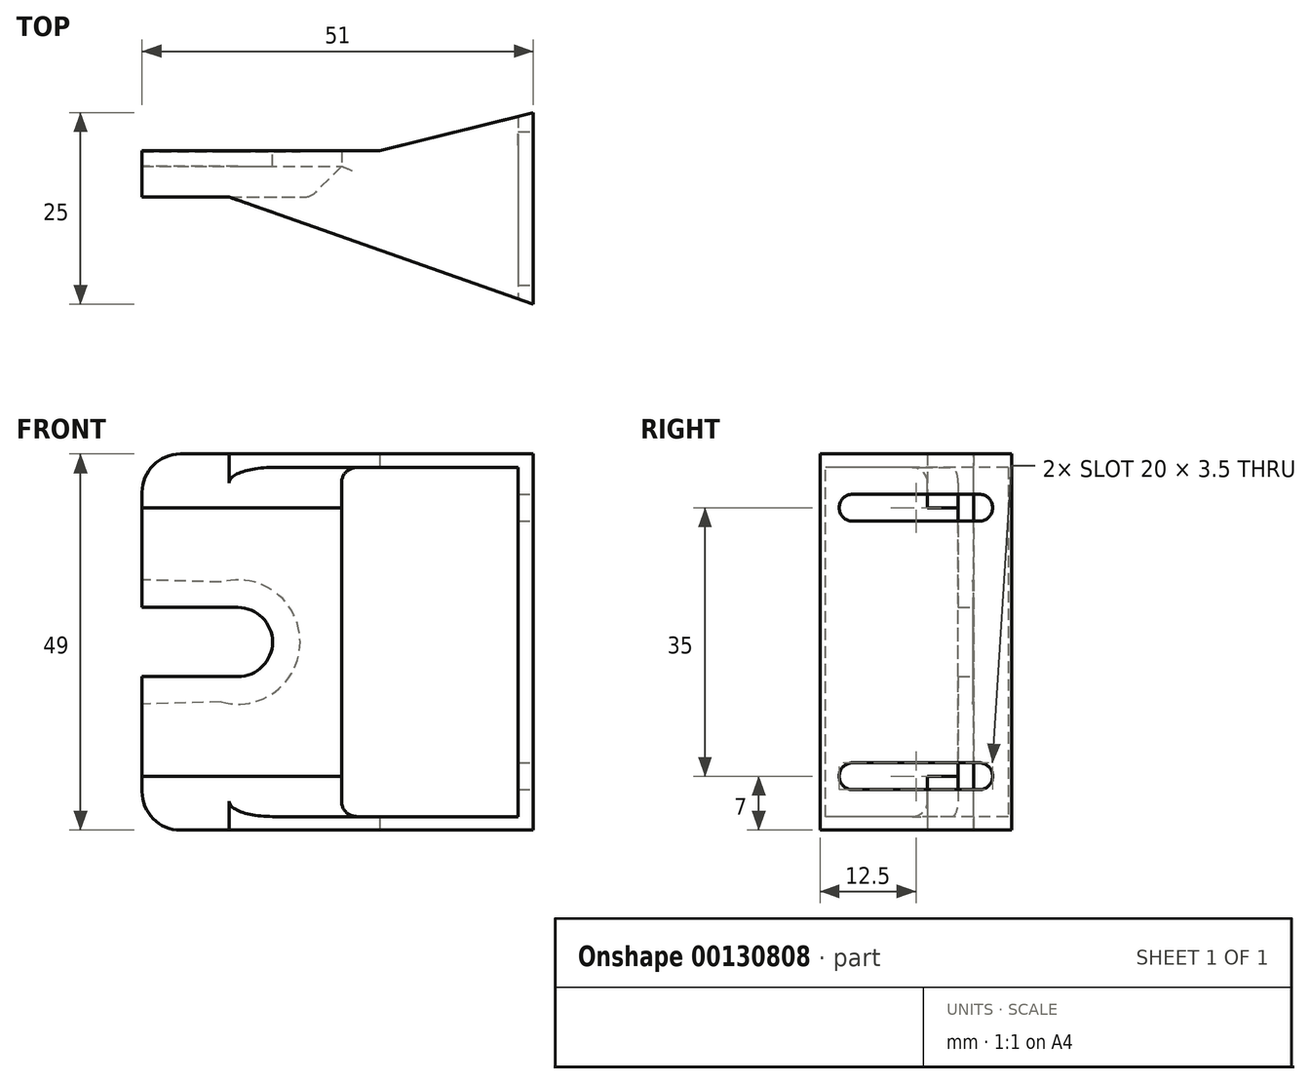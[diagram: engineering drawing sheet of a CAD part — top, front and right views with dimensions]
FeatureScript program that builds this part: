
annotation { "Feature Type Name" : "Feature", "Feature Type Description" : "" }
export const myFeature = defineFeature(function(context is Context, id is Id, definition is map)
    precondition{}
    {
        {
            var Q0;
            Q0=qCreatedBy(makeId("Top.planeOp"),FACE);
            var sketch = newSketch(context, id + "F0", { "sketchPlane" : qUnion([Q0])});
            skLineSegment(sketch, "E0.bottom", {"start": v(0, 2) * mm, "end": v(51, 2) * mm});
            skLineSegment(sketch, "E0.top", {"start": v(0, 0) * mm, "end": v(0, 0) * mm});
            skLineSegment(sketch, "E0.left", {"start": v(0, 2) * mm, "end": v(0, 0) * mm});
            skLineSegment(sketch, "E1", {"start": v(51, 2) * mm, "end": v(51, -18) * mm});
            skLineSegment(sketch, "E2", {"start": v(0, 0) * mm, "end": v(51, -18) * mm});
            skLineSegment(sketch, "E3", {"start": v(51, 2) * mm, "end": v(51, 7) * mm});
            skLineSegment(sketch, "E4", {"start": v(51, 7) * mm, "end": v(31, 2) * mm});
            skSolve(sketch);
        }
        {
            var Q0;
            Q0=makeQuery(id+"F0.imprint","IMPRINT",FACE,{"disambiguationData":[TD([[makeQuery(id+"F0.imprint","IMPRINT",EDGE,{"derivedFrom":sQuery(id+"F0.wireOp",EDGE,"E0.bottom")}),-1.0]])]});
            var Q1;
            {var subQ0=sQuery(id+"F0.wireOp",EDGE,"SCWSvQnW-zgxt-xv1m-XBCz-Pb8vfzgxZMeU");Q1=makeQuery(id+"F0.imprint","IMPRINT",FACE,{"disambiguationData":[TD([[makeQuery(id+"F0.imprint","IMPRINT",EDGE,{"derivedFrom":subQ0}),-1.0]])]});}
            var Q2;
            {var subQ0=sQuery(id+"F0.wireOp",EDGE,"E3");Q2=makeQuery(id+"F0.imprint","IMPRINT",FACE,{"disambiguationData":[TD([[makeQuery(id+"F0.imprint","IMPRINT",EDGE,{"derivedFrom":subQ0}),1.0]])]});}
            extrude(context, id + "F1", {"entities" : qUnion([Q0, Q1, Q2]), "depth" : 49 * mm});
        }
        {
            var Q0;
            Q0=makeQuery(id+"F1.opExtrude","SWEPT_FACE",FACE,{"disambiguationData":[OSD([sQuery(id+"F0.wireOp",EDGE,"E0.bottom")])]});
            var sketch = newSketch(context, id + "F2", { "sketchPlane" : qUnion([Q0])});
            skArc(sketch, "E5", {"start": v(-12.5, 29) * mm, "mid": v(-17, 24.5) * mm, "end": v(-12.5, 20) * mm});
            skPoint(sketch, "E5.centerSnap0", {"position": v(0, 24.5) * mm});
            skLineSegment(sketch, "E6.bottom", {"start": v(-12.5, 20) * mm, "end": v(0.01, 20) * mm});
            skLineSegment(sketch, "E6.top", {"start": v(-12.5, 29) * mm, "end": v(0, 29) * mm});
            skLineSegment(sketch, "E6.right", {"start": v(0.01, 20) * mm, "end": v(0, 29) * mm});
            skSolve(sketch);
        }
        {
            var Q0;
            Q0=makeQuery(id+"F2.imprint","IMPRINT",FACE,{"disambiguationData":[TD([[makeQuery(id+"F2.imprint","IMPRINT",EDGE,{"derivedFrom":sQuery(id+"F2.wireOp",EDGE,"E5")}),1.0]])]});
            extrude(context, id + "F3", {"entities" : qUnion([Q0]), "operationType" : NewBodyOperationType.REMOVE, "endBound" : BoundingType.UP_TO_NEXT, "oppositeDirection" : true, "depth" : 25 * mm});
        }
        {
            var Q0;
            Q0=makeQuery(id+"F1.opExtrude","SWEPT_FACE",FACE,{"disambiguationData":[OSD([sQuery(id+"F0.wireOp",EDGE,"E0.bottom")])]});
            var sketch = newSketch(context, id + "F4", { "sketchPlane" : qUnion([Q0])});
            skLineSegment(sketch, "E7.bottom", {"start": v(-49, 47.25) * mm, "end": v(-26, 47.25) * mm});
            skLineSegment(sketch, "E7.top", {"start": v(-49, 1.75) * mm, "end": v(-26, 1.75) * mm});
            skLineSegment(sketch, "E7.left", {"start": v(-49, 47.25) * mm, "end": v(-49, 1.75) * mm});
            skLineSegment(sketch, "E7.right", {"start": v(-26, 47.25) * mm, "end": v(-26, 1.75) * mm});
            skSolve(sketch);
        }
        {
            var Q0;
            Q0=makeQuery(id+"F4.imprint","IMPRINT",FACE,{"disambiguationData":[TD([[makeQuery(id+"F4.imprint","IMPRINT",EDGE,{"derivedFrom":sQuery(id+"F4.wireOp",EDGE,"E7.bottom")}),-1.0]])]});
            extrude(context, id + "F5", {"entities" : qUnion([Q0]), "operationType" : NewBodyOperationType.REMOVE, "endBound" : BoundingType.SYMMETRIC, "depth" : 50 * mm});
        }
        {
            var Q0;
            Q0=makeQuery(id+"F1.opExtrude","SWEPT_FACE",FACE,{"disambiguationData":[OSD([sQuery(id+"F0.wireOp",EDGE,"E1")])]});
            var sketch = newSketch(context, id + "F6", { "sketchPlane" : qUnion([Q0])});
            skCircle(sketch, "E8", {"center": v(2.75, 42) * mm, "radius": 1.75 * mm});
            skCircle(sketch, "E9", {"center": v(-13.75, 42) * mm, "radius": 1.75 * mm});
            skCircle(sketch, "E10", {"center": v(2.75, 7) * mm, "radius": 1.75 * mm});
            skCircle(sketch, "E11", {"center": v(-13.75, 7) * mm, "radius": 1.75 * mm});
            skLineSegment(sketch, "E12", {"start": v(2.75, 7) * mm, "end": v(2.75, 42) * mm});
            skLineSegment(sketch, "E13", {"start": v(7, 24.5) * mm, "end": v(2.75, 24.5) * mm});
            skPoint(sketch, "E13.endSnap0", {"position": v(7, 24.5) * mm});
            skLineSegment(sketch, "E14", {"start": v(-13.75, 5.25) * mm, "end": v(2.75, 5.25) * mm});
            skLineSegment(sketch, "E15", {"start": v(-13.75, 8.75) * mm, "end": v(2.75, 8.75) * mm});
            skLineSegment(sketch, "E16", {"start": v(2.75, 40.25) * mm, "end": v(-13.75, 40.25) * mm});
            skLineSegment(sketch, "E17", {"start": v(2.75, 43.75) * mm, "end": v(-13.75, 43.75) * mm});
            skSolve(sketch);
        }
        {
            var Q0;
            {var subQ0=sQuery(id+"F6.wireOp",EDGE,"E16");Q0=makeQuery(id+"F6.imprint","IMPRINT",FACE,{"disambiguationData":[TD([[makeQuery(id+"F6.imprint","IMPRINT",EDGE,{"derivedFrom":subQ0}),-1.0]])]});}
            var Q1;
            {var subQ0=sQuery(id+"F6.wireOp",EDGE,"E9");var subQ1=makeQuery(id+"F6.imprint","INTERSECT",VERTEX,{"derivedFrom":[subQ0,sQuery(id+"F6.wireOp",EDGE,"E16")]});Q1=makeQuery(id+"F6.imprint","IMPRINT",FACE,{"disambiguationData":[TD([[makeQuery(id+"F6.imprint","IMPRINT",EDGE,{"disambiguationData":[TD([[subQ1,1.0]])],"derivedFrom":subQ0}),1.0]])]});}
            var Q2;
            {var subQ0=sQuery(id+"F6.wireOp",EDGE,"E8");var subQ1=makeQuery(id+"F6.imprint","INTERSECT",VERTEX,{"derivedFrom":[subQ0,sQuery(id+"F6.wireOp",EDGE,"E16")]});Q2=makeQuery(id+"F6.imprint","IMPRINT",FACE,{"disambiguationData":[TD([[makeQuery(id+"F6.imprint","IMPRINT",EDGE,{"disambiguationData":[TD([[subQ1,1.0]])],"derivedFrom":subQ0}),1.0]])]});}
            var Q3;
            {var subQ0=sQuery(id+"F6.wireOp",EDGE,"E14");Q3=makeQuery(id+"F6.imprint","IMPRINT",FACE,{"disambiguationData":[TD([[makeQuery(id+"F6.imprint","IMPRINT",EDGE,{"derivedFrom":subQ0}),1.0]])]});}
            var Q4;
            {var subQ0=sQuery(id+"F6.wireOp",EDGE,"E11");var subQ1=makeQuery(id+"F6.imprint","INTERSECT",VERTEX,{"derivedFrom":[subQ0,sQuery(id+"F6.wireOp",EDGE,"E14")]});Q4=makeQuery(id+"F6.imprint","IMPRINT",FACE,{"disambiguationData":[TD([[makeQuery(id+"F6.imprint","IMPRINT",EDGE,{"disambiguationData":[TD([[subQ1,1.0]])],"derivedFrom":subQ0}),1.0]])]});}
            var Q5;
            {var subQ0=sQuery(id+"F6.wireOp",EDGE,"E10");var subQ1=makeQuery(id+"F6.imprint","INTERSECT",VERTEX,{"derivedFrom":[subQ0,sQuery(id+"F6.wireOp",EDGE,"E14")]});Q5=makeQuery(id+"F6.imprint","IMPRINT",FACE,{"disambiguationData":[TD([[makeQuery(id+"F6.imprint","IMPRINT",EDGE,{"disambiguationData":[TD([[subQ1,1.0]])],"derivedFrom":subQ0}),1.0]])]});}
            extrude(context, id + "F7", {"entities" : qUnion([Q0, Q1, Q2, Q3, Q4, Q5]), "operationType" : NewBodyOperationType.REMOVE, "endBound" : BoundingType.UP_TO_NEXT, "oppositeDirection" : true, "depth" : 25 * mm});
        }
        {
            var Q0;
            Q0=qCreatedBy(makeId("Front.planeOp"),FACE);
            var sketch = newSketch(context, id + "F8", { "sketchPlane" : qUnion([Q0])});
            skLineSegment(sketch, "E18.bottom", {"start": v(31.05, 47.25) * mm, "end": v(-2.7, 47.25) * mm});
            skLineSegment(sketch, "E18.top", {"start": v(31.05, 1.75) * mm, "end": v(-2.7, 1.75) * mm});
            skLineSegment(sketch, "E18.left", {"start": v(31.05, 47.25) * mm, "end": v(31.05, 1.75) * mm});
            skLineSegment(sketch, "E18.right", {"start": v(-2.7, 47.25) * mm, "end": v(-2.7, 1.75) * mm});
            skSolve(sketch);
        }
        {
            var Q0;
            Q0=qSketchRegion(id+"F8",true);
            extrude(context, id + "F9", {"entities" : qUnion([Q0]), "operationType" : NewBodyOperationType.REMOVE, "endBound" : BoundingType.THROUGH_ALL, "depth" : 25 * mm});
        }
        {
            var Q0;
            {var subQ3=sQuery(id+"F2.wireOp",EDGE,"E5");Q0=makeQuery(id+"F2.imprint","IMPRINT",FACE,{"disambiguationData":[TD([[makeQuery(id+"F2.imprint","IMPRINT",EDGE,{"derivedFrom":subQ3}),-1.0]])]});}
            var sketch = newSketch(context, id + "F10", { "sketchPlane" : qUnion([Q0])});
            skCircle(sketch, "E19", {"center": v(-12.5, 24.5) * mm, "radius": 8.1 * mm});
            skLineSegment(sketch, "E20", {"start": v(-10.32, 32.3) * mm, "end": v(0, 32.6) * mm});
            skLineSegment(sketch, "E21", {"start": v(-10.32, 16.7) * mm, "end": v(0, 16.4) * mm});
            skLineSegment(sketch, "E22", {"start": v(0, 16.4) * mm, "end": v(0, 32.6) * mm});
            skSolve(sketch);
        }
        {
            var Q0;
            Q0=qSketchRegion(id+"F10",true);
            extrude(context, id + "F11", {"entities" : qUnion([Q0]), "operationType" : NewBodyOperationType.REMOVE, "oppositeDirection" : true, "depth" : 0.1 * mm});
        }
        {
            var Q0;
            Q0=makeQuery(id+"F9.boolean.opBoolean","COPY",FACE,{"derivedFrom":makeQuery(id+"F9.opExtrude","CAP_FACE",FACE,{"disambiguationData":[OSD([sQuery(id+"F8.wireOp",EDGE,"E18.bottom"),sQuery(id+"F8.wireOp",EDGE,"E18.top"),sQuery(id+"F8.wireOp",EDGE,"E18.left"),sQuery(id+"F8.wireOp",EDGE,"E18.right")])],"isStart":true})});
            var sketch = newSketch(context, id + "F12", { "sketchPlane" : qUnion([Q0])});
            skLineSegment(sketch, "E23.bottom", {"start": v(0, 49) * mm, "end": v(26, 49) * mm});
            skLineSegment(sketch, "E23.top", {"start": v(0, 42) * mm, "end": v(26, 42) * mm});
            skLineSegment(sketch, "E23.left", {"start": v(0, 49) * mm, "end": v(0, 42) * mm});
            skLineSegment(sketch, "E23.right", {"start": v(26, 49) * mm, "end": v(26, 42) * mm});
            skLineSegment(sketch, "E24.bottom", {"start": v(0, 7) * mm, "end": v(26, 7) * mm});
            skLineSegment(sketch, "E24.top", {"start": v(0, 0) * mm, "end": v(26, 0) * mm});
            skLineSegment(sketch, "E24.left", {"start": v(0, 7) * mm, "end": v(0, 0) * mm});
            skLineSegment(sketch, "E24.right", {"start": v(26, 7) * mm, "end": v(26, 0) * mm});
            skLineSegment(sketch, "E25", {"start": v(0, 42) * mm, "end": v(0, 7) * mm});
            skLineSegment(sketch, "E26", {"start": v(17, 24.5) * mm, "end": v(0, 24.5) * mm});
            skSolve(sketch);
        }
        {
            var Q0;
            {var subQ0=sQuery(id+"F12.wireOp",EDGE,"E23.bottom");Q0=makeQuery(id+"F12.imprint","IMPRINT",FACE,{"disambiguationData":[TD([[makeQuery(id+"F12.imprint","IMPRINT",EDGE,{"derivedFrom":subQ0}),-1.0]])]});}
            var Q1;
            {var subQ0=sQuery(id+"F12.wireOp",EDGE,"E24.top");Q1=makeQuery(id+"F12.imprint","IMPRINT",FACE,{"disambiguationData":[TD([[makeQuery(id+"F12.imprint","IMPRINT",EDGE,{"derivedFrom":subQ0}),1.0]])]});}
            var Q2;
            {var subQ0=sQuery(id+"F12.wireOp",EDGE,"E23.top");Q2=makeQuery(id+"F12.imprint","IMPRINT",FACE,{"disambiguationData":[TD([[makeQuery(id+"F12.imprint","IMPRINT",EDGE,{"derivedFrom":subQ0}),1.0]])]});}
            var Q3;
            {var subQ0=sQuery(id+"F12.wireOp",EDGE,"E24.bottom");Q3=makeQuery(id+"F12.imprint","IMPRINT",FACE,{"disambiguationData":[TD([[makeQuery(id+"F12.imprint","IMPRINT",EDGE,{"derivedFrom":subQ0}),-1.0]])]});}
            extrude(context, id + "F13", {"entities" : qUnion([Q0, Q1, Q2, Q3]), "operationType" : NewBodyOperationType.ADD, "depth" : 4 * mm});
        }
        {
            var Q0;
            Q0=makeQuery(id+"F13.opExtrude","CAP_EDGE",EDGE,{"disambiguationData":[OSD([sQuery(id+"F12.wireOp",EDGE,"E24.right")])],"isStart":false});
            var Q1;
            Q1=makeQuery(id+"F13.opExtrude","CAP_EDGE",EDGE,{"disambiguationData":[OSD([sQuery(id+"F12.wireOp",EDGE,"E23.right")])],"isStart":false});
            chamfer(context, id + "F14", {"entities" : qUnion([Q0, Q1]), "width" : 4 * mm, "tangentPropagation" : true});
        }
        {
            var Q0;
            Q0=makeQuery(id+"F13.boolean.opBoolean","INTERSECT",EDGE,{"derivedFrom":[makeQuery(id+"F9.boolean.opBoolean","MERGE",FACE,{"derivedFrom":[makeQuery(id+"F5.boolean.opBoolean","COPY",FACE,{"derivedFrom":makeQuery(id+"F5.opExtrude","SWEPT_FACE",FACE,{"disambiguationData":[OSD([sQuery(id+"F4.wireOp",EDGE,"E7.top")])]})}),makeQuery(id+"F9.opExtrude","SWEPT_FACE",FACE,{"disambiguationData":[OSD([sQuery(id+"F8.wireOp",EDGE,"E18.top")])]})]}),makeQuery(id+"F13.opExtrude","CAP_FACE",FACE,{"disambiguationData":[OSD([sQuery(id+"F12.wireOp",EDGE,"E24.bottom"),sQuery(id+"F12.wireOp",EDGE,"E24.top"),sQuery(id+"F12.wireOp",EDGE,"E24.left"),sQuery(id+"F12.wireOp",EDGE,"E24.right")])],"isStart":false})]});
            var Q1;
            Q1=makeQuery(id+"F13.boolean.opBoolean","INTERSECT",EDGE,{"derivedFrom":[makeQuery(id+"F9.boolean.opBoolean","MERGE",FACE,{"derivedFrom":[makeQuery(id+"F5.boolean.opBoolean","COPY",FACE,{"derivedFrom":makeQuery(id+"F5.opExtrude","SWEPT_FACE",FACE,{"disambiguationData":[OSD([sQuery(id+"F4.wireOp",EDGE,"E7.bottom")])]})}),makeQuery(id+"F9.opExtrude","SWEPT_FACE",FACE,{"disambiguationData":[OSD([sQuery(id+"F8.wireOp",EDGE,"E18.bottom")])]})]}),makeQuery(id+"F13.opExtrude","CAP_FACE",FACE,{"disambiguationData":[OSD([sQuery(id+"F12.wireOp",EDGE,"E23.bottom"),sQuery(id+"F12.wireOp",EDGE,"E23.top"),sQuery(id+"F12.wireOp",EDGE,"E23.left"),sQuery(id+"F12.wireOp",EDGE,"E23.right")])],"isStart":false})]});
            var Q2;
            Q2=makeQuery(id+"F14.opChamfer","BLEND_EDGE",EDGE,{"blendedFrom":[makeQuery(id+"F13.opExtrude","CAP_EDGE",EDGE,{"disambiguationData":[OSD([sQuery(id+"F12.wireOp",EDGE,"E23.right")])],"isStart":false}),makeQuery(id+"F9.boolean.opBoolean","MERGE",FACE,{"derivedFrom":[makeQuery(id+"F5.boolean.opBoolean","COPY",FACE,{"derivedFrom":makeQuery(id+"F5.opExtrude","SWEPT_FACE",FACE,{"disambiguationData":[OSD([sQuery(id+"F4.wireOp",EDGE,"E7.bottom")])]})}),makeQuery(id+"F9.opExtrude","SWEPT_FACE",FACE,{"disambiguationData":[OSD([sQuery(id+"F8.wireOp",EDGE,"E18.bottom")])]})]})],"blendedInto":[makeQuery(id+"F9.boolean.opBoolean","MERGE",FACE,{"derivedFrom":[makeQuery(id+"F5.boolean.opBoolean","COPY",FACE,{"derivedFrom":makeQuery(id+"F5.opExtrude","SWEPT_FACE",FACE,{"disambiguationData":[OSD([sQuery(id+"F4.wireOp",EDGE,"E7.bottom")])]})}),makeQuery(id+"F9.opExtrude","SWEPT_FACE",FACE,{"disambiguationData":[OSD([sQuery(id+"F8.wireOp",EDGE,"E18.bottom")])]})]})]});
            var Q3;
            Q3=makeQuery(id+"F14.opChamfer","BLEND_EDGE",EDGE,{"blendedFrom":[makeQuery(id+"F13.opExtrude","CAP_EDGE",EDGE,{"disambiguationData":[OSD([sQuery(id+"F12.wireOp",EDGE,"E24.right")])],"isStart":false}),makeQuery(id+"F9.boolean.opBoolean","MERGE",FACE,{"derivedFrom":[makeQuery(id+"F5.boolean.opBoolean","COPY",FACE,{"derivedFrom":makeQuery(id+"F5.opExtrude","SWEPT_FACE",FACE,{"disambiguationData":[OSD([sQuery(id+"F4.wireOp",EDGE,"E7.top")])]})}),makeQuery(id+"F9.opExtrude","SWEPT_FACE",FACE,{"disambiguationData":[OSD([sQuery(id+"F8.wireOp",EDGE,"E18.top")])]})]})],"blendedInto":[makeQuery(id+"F9.boolean.opBoolean","MERGE",FACE,{"derivedFrom":[makeQuery(id+"F5.boolean.opBoolean","COPY",FACE,{"derivedFrom":makeQuery(id+"F5.opExtrude","SWEPT_FACE",FACE,{"disambiguationData":[OSD([sQuery(id+"F4.wireOp",EDGE,"E7.top")])]})}),makeQuery(id+"F9.opExtrude","SWEPT_FACE",FACE,{"disambiguationData":[OSD([sQuery(id+"F8.wireOp",EDGE,"E18.top")])]})]})]});
            var Q4;
            {var subQ0=sQuery(id+"F12.wireOp",EDGE,"E24.right");Q4=makeQuery(id+"F14.opChamfer","BLEND_EDGE",EDGE,{"blendedFrom":[makeQuery(id+"F13.opExtrude","CAP_EDGE",EDGE,{"disambiguationData":[OSD([subQ0])],"isStart":false}),makeQuery(id+"F13.opExtrude","CAP_FACE",FACE,{"disambiguationData":[OSD([sQuery(id+"F12.wireOp",EDGE,"E24.bottom"),sQuery(id+"F12.wireOp",EDGE,"E24.top"),sQuery(id+"F12.wireOp",EDGE,"E24.left"),subQ0])],"isStart":false})],"blendedInto":[makeQuery(id+"F13.opExtrude","CAP_FACE",FACE,{"disambiguationData":[OSD([sQuery(id+"F12.wireOp",EDGE,"E24.bottom"),sQuery(id+"F12.wireOp",EDGE,"E24.top"),sQuery(id+"F12.wireOp",EDGE,"E24.left"),subQ0])],"isStart":false})]});}
            var Q5;
            {var subQ0=sQuery(id+"F12.wireOp",EDGE,"E23.right");Q5=makeQuery(id+"F14.opChamfer","BLEND_EDGE",EDGE,{"blendedFrom":[makeQuery(id+"F13.opExtrude","CAP_EDGE",EDGE,{"disambiguationData":[OSD([subQ0])],"isStart":false}),makeQuery(id+"F13.opExtrude","CAP_FACE",FACE,{"disambiguationData":[OSD([sQuery(id+"F12.wireOp",EDGE,"E23.bottom"),sQuery(id+"F12.wireOp",EDGE,"E23.top"),sQuery(id+"F12.wireOp",EDGE,"E23.left"),subQ0])],"isStart":false})],"blendedInto":[makeQuery(id+"F13.opExtrude","CAP_FACE",FACE,{"disambiguationData":[OSD([sQuery(id+"F12.wireOp",EDGE,"E23.bottom"),sQuery(id+"F12.wireOp",EDGE,"E23.top"),sQuery(id+"F12.wireOp",EDGE,"E23.left"),subQ0])],"isStart":false})]});}
            var Q6;
            Q6=makeQuery(id+"F13.boolean.opBoolean","INTERSECT",EDGE,{"derivedFrom":[makeQuery(id+"F9.boolean.opBoolean","MERGE",FACE,{"derivedFrom":[makeQuery(id+"F5.boolean.opBoolean","COPY",FACE,{"derivedFrom":makeQuery(id+"F5.opExtrude","SWEPT_FACE",FACE,{"disambiguationData":[OSD([sQuery(id+"F4.wireOp",EDGE,"E7.top")])]})}),makeQuery(id+"F9.opExtrude","SWEPT_FACE",FACE,{"disambiguationData":[OSD([sQuery(id+"F8.wireOp",EDGE,"E18.top")])]})]}),makeQuery(id+"F13.opExtrude","SWEPT_FACE",FACE,{"disambiguationData":[OSD([sQuery(id+"F12.wireOp",EDGE,"E24.right")])]})]});
            var Q7;
            Q7=makeQuery(id+"F13.boolean.opBoolean","INTERSECT",EDGE,{"derivedFrom":[makeQuery(id+"F9.boolean.opBoolean","MERGE",FACE,{"derivedFrom":[makeQuery(id+"F5.boolean.opBoolean","COPY",FACE,{"derivedFrom":makeQuery(id+"F5.opExtrude","SWEPT_FACE",FACE,{"disambiguationData":[OSD([sQuery(id+"F4.wireOp",EDGE,"E7.bottom")])]})}),makeQuery(id+"F9.opExtrude","SWEPT_FACE",FACE,{"disambiguationData":[OSD([sQuery(id+"F8.wireOp",EDGE,"E18.bottom")])]})]}),makeQuery(id+"F13.opExtrude","SWEPT_FACE",FACE,{"disambiguationData":[OSD([sQuery(id+"F12.wireOp",EDGE,"E23.right")])]})]});
            fillet(context, id + "F15", {"entities" : qUnion([Q0, Q1, Q2, Q3, Q4, Q5, Q6, Q7]), "radius" : 2 * mm, "tangentPropagation" : true, "allowEdgeOverflow" : false});
        }
        {
            var Q0;
            Q0=makeQuery(id+"F13.boolean.opBoolean","MERGE",EDGE,{"derivedFrom":[makeQuery(id+"F1.opExtrude","CAP_EDGE",EDGE,{"disambiguationData":[OSD([sQuery(id+"F0.wireOp",EDGE,"E0.left")])],"isStart":false}),makeQuery(id+"F13.opExtrude","SWEPT_EDGE",EDGE,{"disambiguationData":[OSD([sQuery(id+"F12.wireOp",EDGE,"E23.bottom"),sQuery(id+"F12.wireOp",EDGE,"E23.left")])]})]});
            var Q1;
            Q1=makeQuery(id+"F13.boolean.opBoolean","MERGE",EDGE,{"derivedFrom":[makeQuery(id+"F1.opExtrude","CAP_EDGE",EDGE,{"disambiguationData":[OSD([sQuery(id+"F0.wireOp",EDGE,"E0.left")])],"isStart":true}),makeQuery(id+"F13.opExtrude","SWEPT_EDGE",EDGE,{"disambiguationData":[OSD([sQuery(id+"F12.wireOp",EDGE,"E24.top"),sQuery(id+"F12.wireOp",EDGE,"E24.left")])]})]});
            fillet(context, id + "F16", {"entities" : qUnion([Q0, Q1]), "radius" : 5 * mm, "tangentPropagation" : true, "allowEdgeOverflow" : false});
        }
    });
